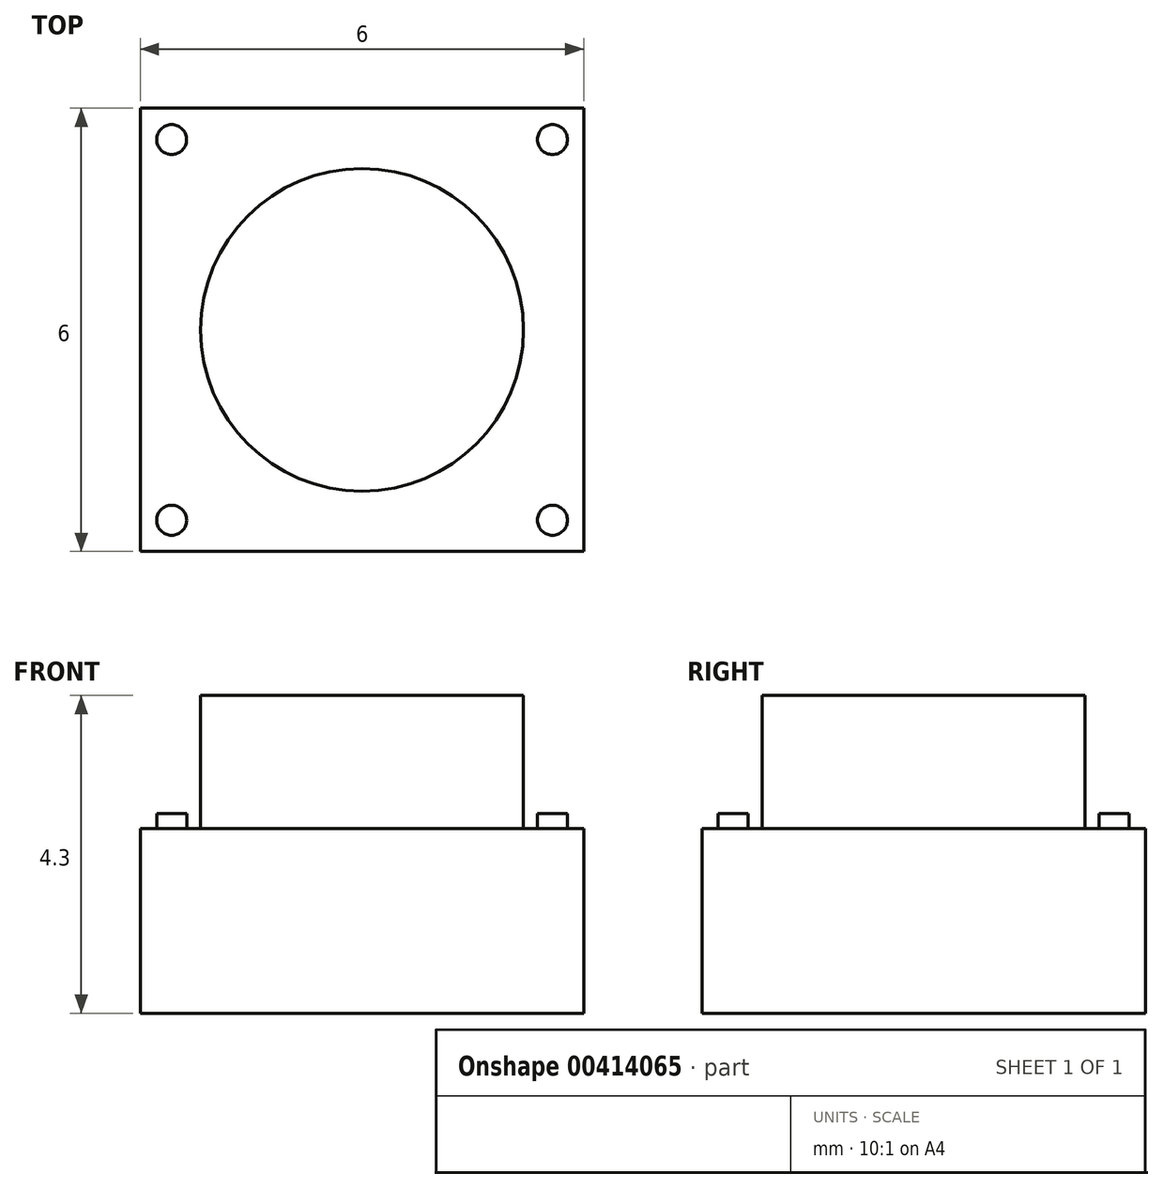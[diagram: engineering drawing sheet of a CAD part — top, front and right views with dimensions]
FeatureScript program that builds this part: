
annotation { "Feature Type Name" : "Feature", "Feature Type Description" : "" }
export const myFeature = defineFeature(function(context is Context, id is Id, definition is map)
    precondition{}
    {
        {
            var Q0;
            Q0=qCreatedBy(makeId("Top.planeOp"),FACE);
            var sketch = newSketch(context, id + "F0", { "sketchPlane" : qUnion([Q0])});
            skLineSegment(sketch, "E0.bottom", {"start": v(0, 0) * mm, "end": v(6, 0) * mm});
            skLineSegment(sketch, "E0.top", {"start": v(0, -6) * mm, "end": v(6, -6) * mm});
            skLineSegment(sketch, "E0.left", {"start": v(0, 0) * mm, "end": v(0, -6) * mm});
            skLineSegment(sketch, "E0.right", {"start": v(6, 0) * mm, "end": v(6, -6) * mm});
            skSolve(sketch);
        }
        {
            var Q0;
            Q0=makeQuery(id+"F0.imprint","IMPRINT",FACE,{"disambiguationData":[TD([[makeQuery(id+"F0.imprint","IMPRINT",EDGE,{"derivedFrom":sQuery(id+"F0.wireOp",EDGE,"E0.bottom")}),-1.0]])]});
            extrude(context, id + "F1", {"entities" : qUnion([Q0]), "depth" : 2.5 * mm});
        }
        {
            var Q0;
            Q0=makeQuery(id+"F1.opExtrude","CAP_FACE",FACE,{"disambiguationData":[OSD([sQuery(id+"F0.wireOp",EDGE,"E0.bottom"),sQuery(id+"F0.wireOp",EDGE,"E0.top"),sQuery(id+"F0.wireOp",EDGE,"E0.left"),sQuery(id+"F0.wireOp",EDGE,"E0.right")])],"isStart":false});
            var sketch = newSketch(context, id + "F2", { "sketchPlane" : qUnion([Q0])});
            skLineSegment(sketch, "E1", {"start": v(0, 0) * mm, "end": v(0.28, -0.28) * mm});
            skLineSegment(sketch, "E2", {"start": v(6, -6) * mm, "end": v(0, -6) * mm});
            skPoint(sketch, "E3.middle", {"position": v(3, -3) * mm});
            skCircle(sketch, "E4", {"center": v(0.42, -0.42) * mm, "radius": 0.2 * mm});
            skCircle(sketch, "E5", {"center": v(5.58, -0.42) * mm, "radius": 0.2 * mm});
            skCircle(sketch, "E6", {"center": v(5.58, -5.58) * mm, "radius": 0.2 * mm});
            skCircle(sketch, "E7", {"center": v(0.42, -5.58) * mm, "radius": 0.2 * mm});
            skCircle(sketch, "E8", {"center": v(3, -3) * mm, "radius": 2.18 * mm});
            skLineSegment(sketch, "E9.trimOffspring", {"start": v(5.72, -5.72) * mm, "end": v(6, -6) * mm});
            skLineSegment(sketch, "E10.trimOffspring", {"start": v(5.58, -0.42) * mm, "end": v(6, 0) * mm});
            skLineSegment(sketch, "E11.trimOffspring", {"start": v(0.42, -0.42) * mm, "end": v(0.57, -0.57) * mm});
            skSolve(sketch);
        }
        {
            var Q0;
            Q0=makeQuery(id+"F2.imprint","IMPRINT",FACE,{"disambiguationData":[TD([[makeQuery(id+"F2.imprint","IMPRINT",EDGE,{"derivedFrom":sQuery(id+"F2.wireOp",EDGE,"E8")}),1.0]])]});
            extrude(context, id + "F3", {"entities" : qUnion([Q0]), "operationType" : NewBodyOperationType.ADD, "depth" : 1.8 * mm});
        }
        {
            var Q0;
            {var subQ0=sQuery(id+"F2.wireOp",EDGE,"E4");var subQ1=makeQuery(id+"F2.imprint","IMPRINT",VERTEX,{"disambiguationData":[OD(0.0)],"derivedFrom":subQ0});Q0=makeQuery(id+"F2.imprint","IMPRINT",FACE,{"disambiguationData":[TD([[makeQuery(id+"F2.imprint","IMPRINT",EDGE,{"disambiguationData":[TD([[subQ1,-1.0]])],"derivedFrom":subQ0}),1.0]])]});}
            var Q1;
            Q1=makeQuery(id+"F2.imprint","IMPRINT",FACE,{"disambiguationData":[TD([[makeQuery(id+"F2.imprint","IMPRINT",EDGE,{"derivedFrom":sQuery(id+"F2.wireOp",EDGE,"E5")}),1.0]])]});
            var Q2;
            Q2=makeQuery(id+"F2.imprint","IMPRINT",FACE,{"disambiguationData":[TD([[makeQuery(id+"F2.imprint","IMPRINT",EDGE,{"derivedFrom":sQuery(id+"F2.wireOp",EDGE,"E6")}),1.0]])]});
            var Q3;
            Q3=makeQuery(id+"F2.imprint","IMPRINT",FACE,{"disambiguationData":[TD([[makeQuery(id+"F2.imprint","IMPRINT",EDGE,{"derivedFrom":sQuery(id+"F2.wireOp",EDGE,"E7")}),1.0]])]});
            extrude(context, id + "F4", {"entities" : qUnion([Q0, Q1, Q2, Q3]), "operationType" : NewBodyOperationType.ADD, "depth" : .2 * mm});
        }
    });
